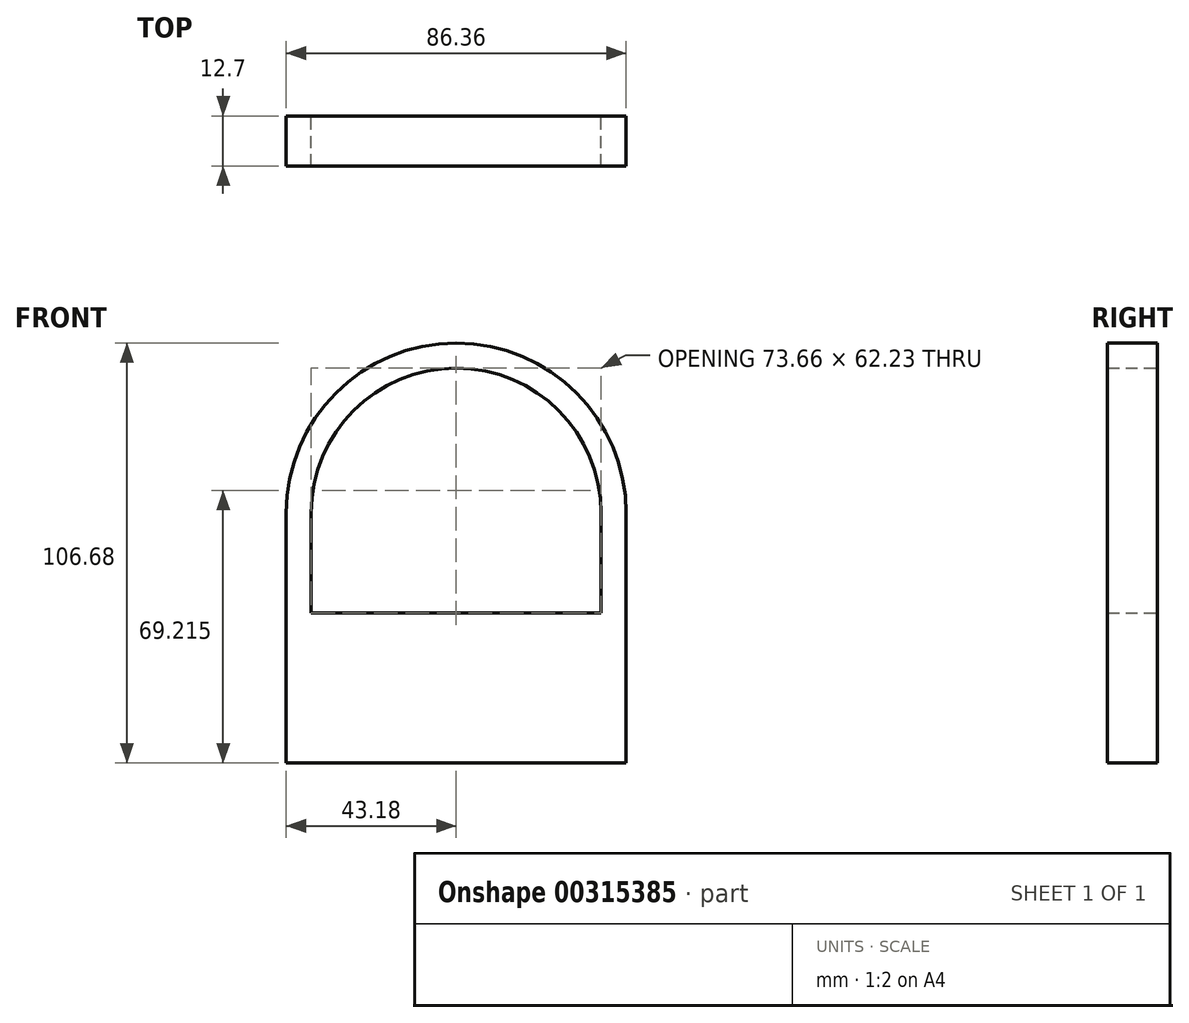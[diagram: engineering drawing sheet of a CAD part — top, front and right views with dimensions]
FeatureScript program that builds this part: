
annotation { "Feature Type Name" : "Feature", "Feature Type Description" : "" }
export const myFeature = defineFeature(function(context is Context, id is Id, definition is map)
    precondition{}
    {
        {
            var Q0;
            Q0=qCreatedBy(makeId("Front.planeOp"),FACE);
            var sketch = newSketch(context, id + "F0", { "sketchPlane" : qUnion([Q0])});
            skLineSegment(sketch, "E0.bottom", {"start": v(-43.18, 19.05) * mm, "end": v(43.18, 19.05) * mm});
            skLineSegment(sketch, "E0.top", {"start": v(-43.18, -19.05) * mm, "end": v(43.18, -19.05) * mm});
            skLineSegment(sketch, "E0.left", {"start": v(-43.18, 19.05) * mm, "end": v(-43.18, -19.05) * mm});
            skLineSegment(sketch, "E0.right", {"start": v(43.18, 19.05) * mm, "end": v(43.18, -19.05) * mm});
            skPoint(sketch, "E0.middle", {"position": v(0, 0) * mm});
            skLineSegment(sketch, "E1", {"start": v(-43.18, 19.05) * mm, "end": v(-43.18, 44.45) * mm});
            skLineSegment(sketch, "E2", {"start": v(43.18, 19.05) * mm, "end": v(43.18, 44.45) * mm});
            skArc(sketch, "E3", {"start": v(-43.18, 44.45) * mm, "mid": v(0, 87.63) * mm, "end": v(43.18, 44.45) * mm});
            skArc(sketch, "E4.0", {"start": v(-36.83, 44.45) * mm, "mid": v(0, 81.28) * mm, "end": v(36.83, 44.45) * mm});
            skLineSegment(sketch, "E5.0", {"start": v(-36.83, 19.05) * mm, "end": v(-36.83, 44.45) * mm});
            skLineSegment(sketch, "E6.0", {"start": v(36.83, 19.05) * mm, "end": v(36.83, 44.45) * mm});
            skSolve(sketch);
        }
        {
            var Q0;
            Q0=makeQuery(id+"F0.imprint","IMPRINT",FACE,{"disambiguationData":[TD([[makeQuery(id+"F0.imprint","IMPRINT",EDGE,{"derivedFrom":sQuery(id+"F0.wireOp",EDGE,"E0.top")}),1.0]])]});
            var Q1;
            {var subQ0=sQuery(id+"F0.wireOp",EDGE,"E1");Q1=makeQuery(id+"F0.imprint","IMPRINT",FACE,{"disambiguationData":[TD([[makeQuery(id+"F0.imprint","IMPRINT",EDGE,{"derivedFrom":subQ0}),-1.0]])]});}
            extrude(context, id + "F1", {"entities" : qUnion([Q0, Q1]), "endBound" : BoundingType.SYMMETRIC, "depth" : 12.7 * mm});
        }
    });
